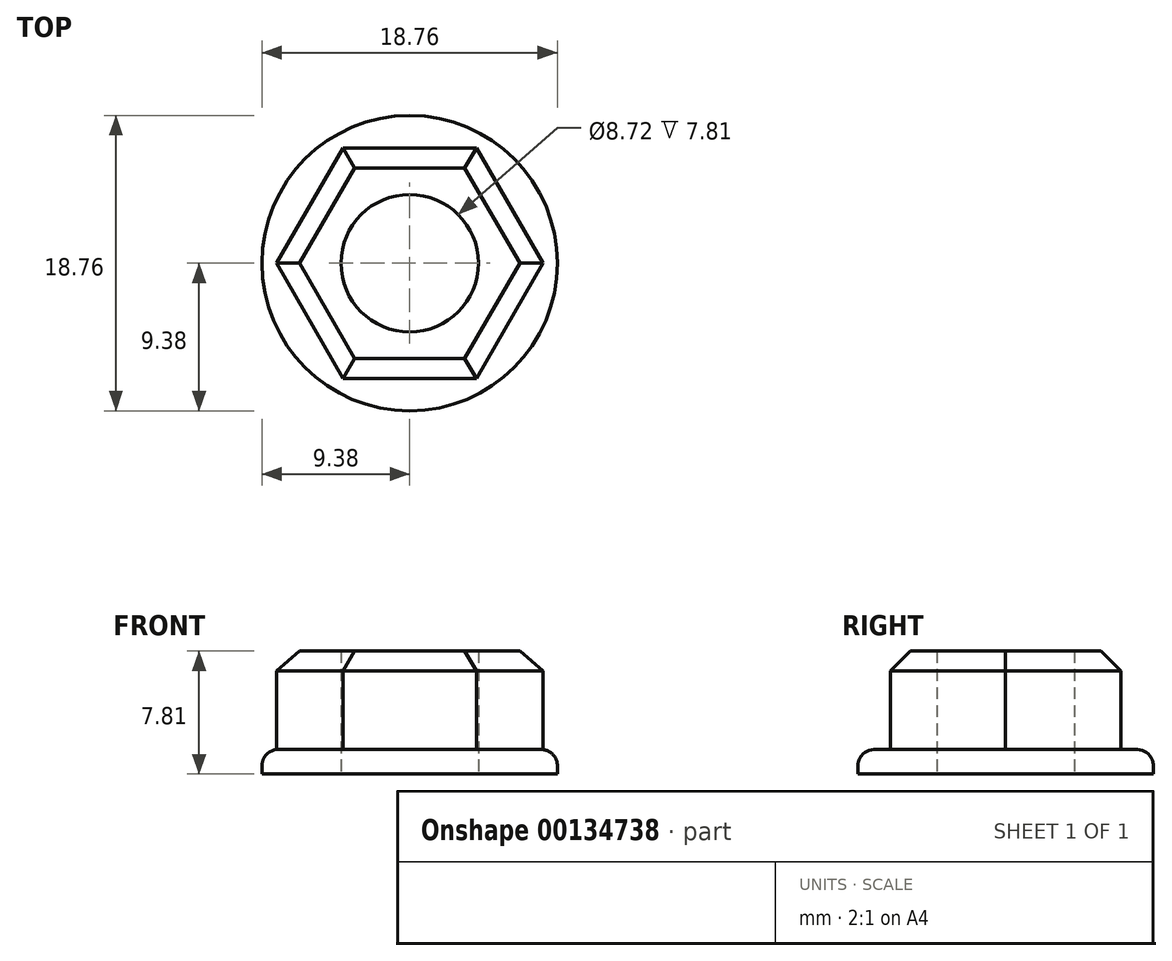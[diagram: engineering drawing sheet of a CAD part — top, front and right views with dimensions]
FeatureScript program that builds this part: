
annotation { "Feature Type Name" : "Feature", "Feature Type Description" : "" }
export const myFeature = defineFeature(function(context is Context, id is Id, definition is map)
    precondition{}
    {
        {
            var Q0;
            Q0=qCreatedBy(makeId("Top.planeOp"),FACE);
            var sketch = newSketch(context, id + "F0", { "sketchPlane" : qUnion([Q0])});
            skLineSegment(sketch, "E0.bottom", {"start": v(-4.23, 7.33) * mm, "end": v(4.23, 7.33) * mm});
            skLineSegment(sketch, "E0.top", {"start": v(-4.23, -7.33) * mm, "end": v(4.23, -7.33) * mm});
            skPoint(sketch, "E0.middle", {"position": v(0, 0) * mm});
            skPoint(sketch, "E1", {"position": v(8.46, 0) * mm});
            skPoint(sketch, "E2", {"position": v(-8.46, 0) * mm});
            skLineSegment(sketch, "E3", {"start": v(-8.46, 0) * mm, "end": v(0, 0) * mm, "construction": true});
            skLineSegment(sketch, "E4", {"start": v(0, 0) * mm, "end": v(8.46, 0) * mm, "construction": true});
            skLineSegment(sketch, "E5", {"start": v(-4.23, 7.33) * mm, "end": v(-8.46, 0) * mm});
            skLineSegment(sketch, "E6", {"start": v(-4.23, -7.33) * mm, "end": v(-8.46, 0) * mm});
            skLineSegment(sketch, "E7", {"start": v(4.23, 7.33) * mm, "end": v(8.46, 0) * mm});
            skLineSegment(sketch, "E8", {"start": v(4.23, -7.33) * mm, "end": v(8.46, 0) * mm});
            skCircle(sketch, "E9", {"center": v(0, 0) * mm, "radius": 9.38 * mm});
            skSolve(sketch);
        }
        {
            var Q0;
            Q0=makeQuery(id+"F0.imprint","IMPRINT",FACE,{"disambiguationData":[TD([[makeQuery(id+"F0.imprint","IMPRINT",EDGE,{"derivedFrom":sQuery(id+"F0.wireOp",EDGE,"E0.bottom")}),-1.0]])]});
            extrude(context, id + "F1", {"entities" : qUnion([Q0]), "depth" : 7.8 * mm});
        }
        {
            var Q0;
            Q0=makeQuery(id+"F0.imprint","IMPRINT",FACE,{"disambiguationData":[TD([[makeQuery(id+"F0.imprint","IMPRINT",EDGE,{"derivedFrom":sQuery(id+"F0.wireOp",EDGE,"E0.bottom")}),1.0]])]});
            extrude(context, id + "F2", {"entities" : qUnion([Q0]), "operationType" : NewBodyOperationType.ADD, "depth" : 1.55 * mm});
        }
        {
            var Q0;
            Q0=makeQuery(id+"F2.opExtrude","CAP_EDGE",EDGE,{"disambiguationData":[OSD([sQuery(id+"F0.wireOp",EDGE,"E9")])],"isStart":false});
            fillet(context, id + "F3", {"entities" : qUnion([Q0]), "radius" : 1.02 * mm, "tangentPropagation" : true, "allowEdgeOverflow" : false});
        }
        {
            var Q0;
            Q0=sQuery(id+"F0.wireOp",VERTEX,"E0.middle");
            var Q1;
            Q1=makeQuery(id+"F1.opExtrude","SWEPT_BODY",BODY,{"disambiguationData":[OSD([sQuery(id+"F0.wireOp",EDGE,"E0.bottom"),sQuery(id+"F0.wireOp",EDGE,"E0.top"),sQuery(id+"F0.wireOp",EDGE,"E5"),sQuery(id+"F0.wireOp",EDGE,"E6"),sQuery(id+"F0.wireOp",EDGE,"E7"),sQuery(id+"F0.wireOp",EDGE,"E8")])]});
            hole(context, id + "F4", {"style" : HoleStyle.SIMPLE, "endStyle" : HoleEndStyle.THROUGH, "oppositeDirection" : true, "holeDiameter" : 8.72 * mm, "startFromSketch" : true, "locations" : qUnion([Q0]), "scope" : qUnion([Q1]), "isTappedThrough" : true});
        }
        {
            var Q0;
            Q0=makeQuery(id+"F4.hole-0.boolean.opBoolean","INTERSECT",EDGE,{"derivedFrom":[makeQuery(id+"F1.opExtrude","CAP_FACE",FACE,{"disambiguationData":[OSD([sQuery(id+"F0.wireOp",EDGE,"E0.bottom"),sQuery(id+"F0.wireOp",EDGE,"E0.top"),sQuery(id+"F0.wireOp",EDGE,"E5"),sQuery(id+"F0.wireOp",EDGE,"E6"),sQuery(id+"F0.wireOp",EDGE,"E7"),sQuery(id+"F0.wireOp",EDGE,"E8")])],"isStart":false}),makeQuery(id+"F4.hole-0.opRevolve","SWEPT_FACE",FACE,{"disambiguationData":[OSD([sQuery(id+"F4.hole-0.sketch.wireOp",EDGE,"core_line_2")])]})]});
            var Q1;
            Q1=makeQuery(id+"F1.opExtrude","CAP_EDGE",EDGE,{"disambiguationData":[OSD([sQuery(id+"F0.wireOp",EDGE,"E0.bottom")])],"isStart":false});
            var Q2;
            Q2=makeQuery(id+"F1.opExtrude","CAP_EDGE",EDGE,{"disambiguationData":[OSD([sQuery(id+"F0.wireOp",EDGE,"E7")])],"isStart":false});
            var Q3;
            Q3=makeQuery(id+"F1.opExtrude","CAP_EDGE",EDGE,{"disambiguationData":[OSD([sQuery(id+"F0.wireOp",EDGE,"E8")])],"isStart":false});
            var Q4;
            Q4=makeQuery(id+"F1.opExtrude","CAP_EDGE",EDGE,{"disambiguationData":[OSD([sQuery(id+"F0.wireOp",EDGE,"E0.top")])],"isStart":false});
            var Q5;
            Q5=makeQuery(id+"F1.opExtrude","CAP_EDGE",EDGE,{"disambiguationData":[OSD([sQuery(id+"F0.wireOp",EDGE,"E6")])],"isStart":false});
            var Q6;
            Q6=makeQuery(id+"F1.opExtrude","CAP_EDGE",EDGE,{"disambiguationData":[OSD([sQuery(id+"F0.wireOp",EDGE,"E5")])],"isStart":false});
            var Q7;
            Q7=makeQuery(id+"F4.hole-0.boolean.opBoolean","COPY",EDGE,{"derivedFrom":makeQuery(id+"F4.hole-0.opRevolve","SWEPT_EDGE",EDGE,{"disambiguationData":[OSD([sQuery(id+"F4.hole-0.sketch.wireOp",EDGE,"core_line_2"),sQuery(id+"F4.hole-0.sketch.wireOp",EDGE,"core_line_3")])]})});
            chamfer(context, id + "F5", {"entities" : qUnion([Q0, Q1, Q2, Q3, Q4, Q5, Q6, Q7]), "width" : 1.27 * mm, "tangentPropagation" : true});
        }
    });
